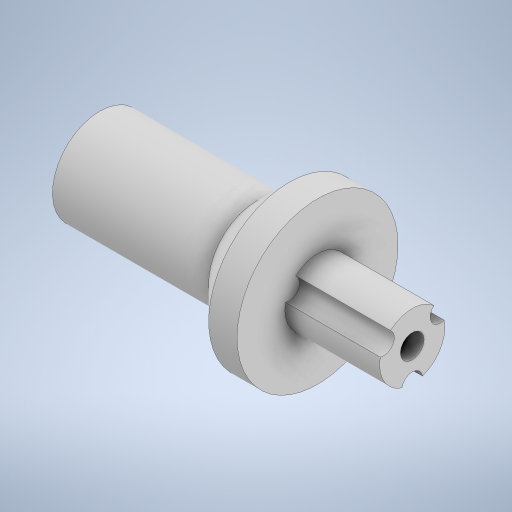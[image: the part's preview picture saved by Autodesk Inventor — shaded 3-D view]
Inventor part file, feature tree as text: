
AUTODESK INVENTOR PART (.ipt)
format: ipt  version: 2023 (Build 270158000, 158)  size: 287,744 bytes
history: native  units: mm
features: extrude x4, sketch x4, other x1, chamfer x1
ambient origin geometry x8: Origin, YZ Plane, XZ Plane, XY Plane, X Axis, Y Axis, Z Axis, Center Point
bodies: Body1 (feature_tree)
feature tree (10):
  other  "Твердое тело1"
  extrude  "Выдавливание1"  Depth=5.2mm
  extrude  "Выдавливание2"  Depth=1.9mm
  extrude  "Выдавливание3"  Depth=10.0mm
  chamfer  "Фаска1"  Distance=20.0mm
  extrude  "Выдавливание4"  Depth=6.9mm
  sketch  "Эскиз1"
  sketch  "Эскиз2"
  sketch  "Эскиз3"
  sketch  "Эскиз4"
